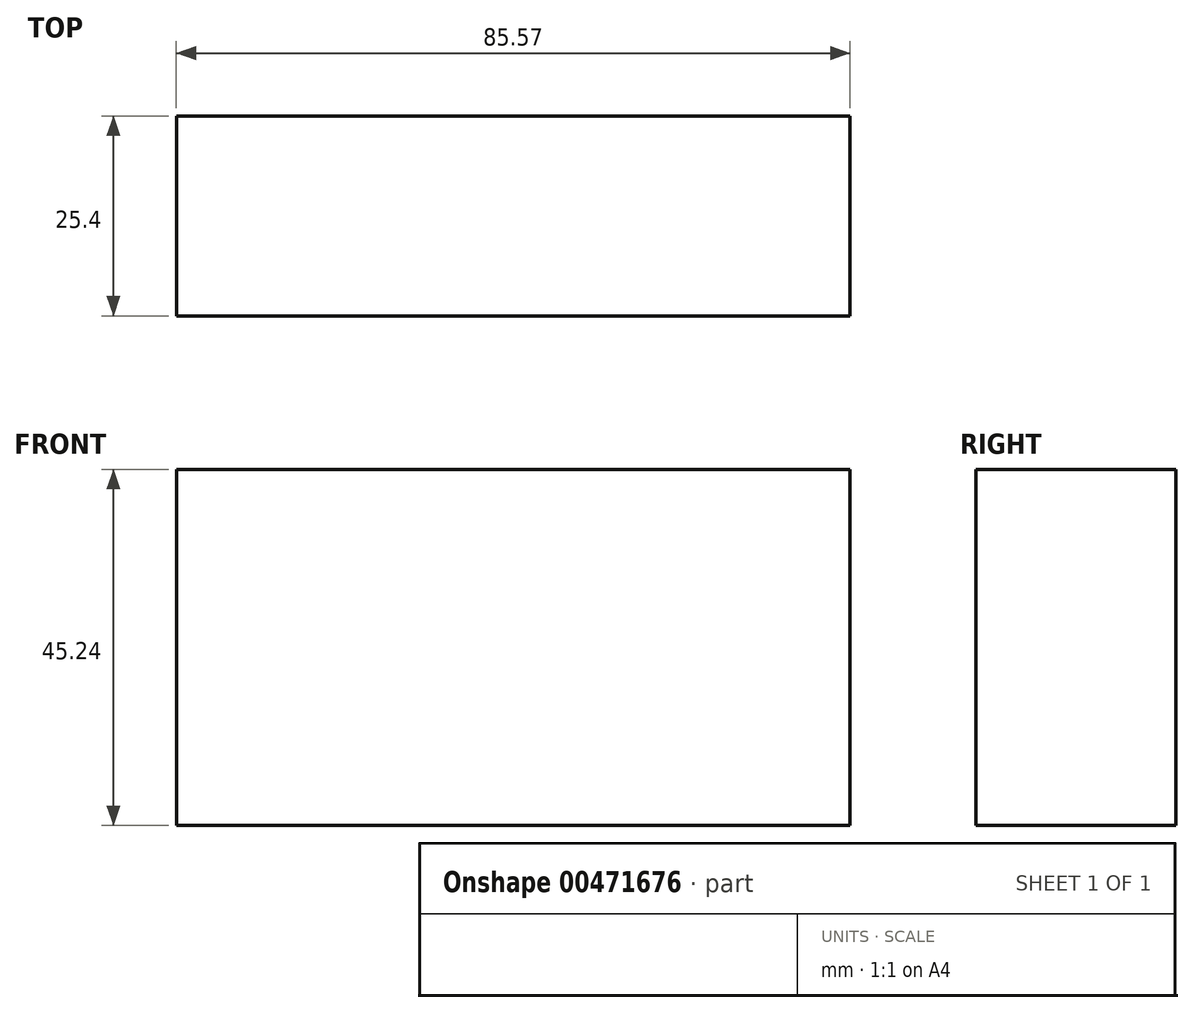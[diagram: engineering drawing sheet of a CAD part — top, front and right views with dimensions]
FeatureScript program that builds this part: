
annotation { "Feature Type Name" : "Feature", "Feature Type Description" : "" }
export const myFeature = defineFeature(function(context is Context, id is Id, definition is map)
    precondition{}
    {
        {
            var Q0;
            Q0=qCreatedBy(makeId("Front.planeOp"),FACE);
            var sketch = newSketch(context, id + "F0", { "sketchPlane" : qUnion([Q0])});
            skLineSegment(sketch, "E0.bottom", {"start": v(-119, 76) * mm, "end": v(-33.44, 76) * mm});
            skLineSegment(sketch, "E0.top", {"start": v(-119, 30.75) * mm, "end": v(-33.44, 30.75) * mm});
            skLineSegment(sketch, "E0.left", {"start": v(-119, 76) * mm, "end": v(-119, 30.75) * mm});
            skLineSegment(sketch, "E0.right", {"start": v(-33.44, 76) * mm, "end": v(-33.44, 30.75) * mm});
            skPoint(sketch, "E0.middle", {"position": v(-76.22, 53.37) * mm});
            skSolve(sketch);
        }
        {
            var Q0;
            Q0 = qSketchRegion(id + "F0", true);
            extrude(context, id + "F1", {"entities" : qUnion([Q0]), "depth" : 25.4 * mm, "offsetDistance" : 25.4 * mm});
        }
    });
